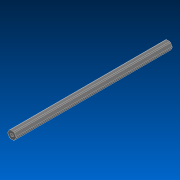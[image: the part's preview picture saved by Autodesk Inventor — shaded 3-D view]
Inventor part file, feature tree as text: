
AUTODESK INVENTOR PART (.ipt)
format: ipt  version: 2022.2 (Build 262287000, 287)  size: 121,856 bytes
history: native  units: in
note: dims shown in document units (in); Inventor stores cm internally (conversion verified against a paired STEP export)
features: extrude x1, sketch x1, other x1
ambient origin geometry x8: Origin, YZ Plane, XZ Plane, XY Plane, X Axis, Y Axis, Z Axis, Center Point
bodies: Solid1 (feature_tree)
feature tree (3):
  extrude  "Extrusion1"  TaperAngle=0.0deg  [1 undecoded]
  sketch  "Sketch1"  dims[d0=25.7in d1=0.0in]
  other  "Cut-Extrude2"
note: 1 required parameter value undecoded (feature->parameter linkage not recoverable at this tier; creation-order binding heuristic only, values carry confidence <= 0.55)
